annotation { "Feature Type Name" : "Feature", "Feature Type Description" : "" }
export const myFeature = defineFeature(function(context is Context, id is Id, definition is map)
    precondition{}
    {
        {
            var Q0;
            Q0=qCreatedBy(makeId("Front.planeOp"),FACE);
            var sketch = newSketch(context, id + "F0", { "sketchPlane" : qUnion([Q0])});
            skLineSegment(sketch, "E0.bottom", {"start": v(50.8, -15.87) * mm, "end": v(-50.8, -15.88) * mm});
            skLineSegment(sketch, "E0.top", {"start": v(50.8, 15.88) * mm, "end": v(-50.8, 15.87) * mm});
            skLineSegment(sketch, "E0.left", {"start": v(50.8, -15.87) * mm, "end": v(50.8, 15.88) * mm});
            skLineSegment(sketch, "E0.right", {"start": v(-50.8, -15.88) * mm, "end": v(-50.8, 15.87) * mm});
            skPoint(sketch, "E0.middle", {"position": v(0, 0) * mm});
            skSolve(sketch);
        }
        {
            var Q0;
            Q0 = qSketchRegion(id + "F0", true);
            var Q1;
            Q1=makeQuery(id+"F0.imprint","IMPRINT",FACE,{"disambiguationData":[TD([[makeQuery(id+"F0.imprint","IMPRINT",EDGE,{"derivedFrom":sQuery(id+"F0.wireOp",EDGE,"E0.bottom")}),-1.0]])]});
            extrude(context, id + "F1", {"entities" : qUnion([Q0, Q1]), "depth" : 152.4 * mm, "offsetDistance" : 25.4 * mm});
        }
        {
            var Q0;
            Q0=makeQuery(id+"F1.opExtrude","CAP_FACE",FACE,{"disambiguationData":[OSD([sQuery(id+"F0.wireOp",EDGE,"E0.bottom"),sQuery(id+"F0.wireOp",EDGE,"E0.top"),sQuery(id+"F0.wireOp",EDGE,"E0.left"),sQuery(id+"F0.wireOp",EDGE,"E0.right")])],"isStart":false});
            var sketch = newSketch(context, id + "F2", { "sketchPlane" : qUnion([Q0])});
            skLineSegment(sketch, "E1", {"start": v(-50.8, 15.87) * mm, "end": v(-50.8, -9.53) * mm});
            skLineSegment(sketch, "E2", {"start": v(50.8, 15.88) * mm, "end": v(50.8, -9.52) * mm});
            skLineSegment(sketch, "E3", {"start": v(44.42, -9.52) * mm, "end": v(10.93, -9.52) * mm});
            skLineSegment(sketch, "E4", {"start": v(-50.8, -9.53) * mm, "end": v(-43.03, -9.53) * mm});
            skLineSegment(sketch, "E5", {"start": v(-43.03, -9.52) * mm, "end": v(-6.12, -9.52) * mm});
            skPoint(sketch, "E6", {"position": v(-43.03, -9.52) * mm});
            skPoint(sketch, "E7", {"position": v(-6.12, -9.52) * mm});
            skPoint(sketch, "E8", {"position": v(10.93, -9.52) * mm});
            skLineSegment(sketch, "E9", {"start": v(-50.8, -9.53) * mm, "end": v(44.42, -9.52) * mm});
            skPoint(sketch, "E10", {"position": v(44.42, -9.52) * mm});
            skLineSegment(sketch, "E11", {"start": v(-43.03, -9.52) * mm, "end": v(-36.68, -15.88) * mm});
            skLineSegment(sketch, "E12", {"start": v(-6.12, -9.52) * mm, "end": v(-12.47, -15.88) * mm});
            skLineSegment(sketch, "E13", {"start": v(10.93, -9.52) * mm, "end": v(17.28, -15.87) * mm});
            skLineSegment(sketch, "E14", {"start": v(44.42, -9.52) * mm, "end": v(38.07, -15.87) * mm});
            skSolve(sketch);
        }
        {
            var Q0;
            {var subQ2=sQuery(id+"F2.wireOp",EDGE,"E13");Q0=makeQuery(id+"F2.imprint","IMPRINT",FACE,{"disambiguationData":[TD([[makeQuery(id+"F2.imprint","IMPRINT",EDGE,{"derivedFrom":subQ2}),1.0]])]});}
            var Q1;
            {var subQ0=sQuery(id+"F2.wireOp",EDGE,"E11");Q1=makeQuery(id+"F2.imprint","IMPRINT",FACE,{"disambiguationData":[TD([[makeQuery(id+"F2.imprint","IMPRINT",EDGE,{"derivedFrom":subQ0}),1.0]])]});}
            extrude(context, id + "F3", {"entities" : qUnion([Q0, Q1]), "operationType" : NewBodyOperationType.REMOVE, "oppositeDirection" : true, "depth" : 19.05 * mm, "offsetDistance" : 25.4 * mm});
        }
        {
            var Q0;
            Q0=makeQuery(id+"F1.opExtrude","CAP_FACE",FACE,{"disambiguationData":[OSD([sQuery(id+"F0.wireOp",EDGE,"E0.bottom"),sQuery(id+"F0.wireOp",EDGE,"E0.top"),sQuery(id+"F0.wireOp",EDGE,"E0.left"),sQuery(id+"F0.wireOp",EDGE,"E0.right")])],"isStart":true});
            var sketch = newSketch(context, id + "F4", { "sketchPlane" : qUnion([Q0])});
            skLineSegment(sketch, "E15", {"start": v(-50.8, 15.88) * mm, "end": v(-50.8, -9.52) * mm});
            skLineSegment(sketch, "E16", {"start": v(-50.8, -9.52) * mm, "end": v(50.8, -9.52) * mm});
            skLineSegment(sketch, "E17", {"start": v(-50.8, -9.52) * mm, "end": v(-45.92, -9.52) * mm});
            skLineSegment(sketch, "E18", {"start": v(-45.92, -9.52) * mm, "end": v(-39.57, -15.87) * mm});
            skLineSegment(sketch, "E19", {"start": v(-50.8, -9.52) * mm, "end": v(-4.88, -9.52) * mm});
            skLineSegment(sketch, "E20", {"start": v(-4.88, -9.52) * mm, "end": v(-11.23, -15.87) * mm});
            skLineSegment(sketch, "E21", {"start": v(-50.8, -9.52) * mm, "end": v(4.88, -9.52) * mm});
            skLineSegment(sketch, "E22", {"start": v(4.88, -9.52) * mm, "end": v(11.23, -15.88) * mm});
            skLineSegment(sketch, "E23", {"start": v(-50.8, -9.52) * mm, "end": v(45.92, -9.52) * mm});
            skLineSegment(sketch, "E24", {"start": v(45.92, -9.52) * mm, "end": v(39.57, -15.88) * mm});
            skSolve(sketch);
        }
        {
            var Q0;
            {var subQ0=sQuery(id+"F4.wireOp",EDGE,"E18");Q0=makeQuery(id+"F4.imprint","IMPRINT",FACE,{"disambiguationData":[TD([[makeQuery(id+"F4.imprint","IMPRINT",EDGE,{"derivedFrom":subQ0}),1.0]])]});}
            var Q1;
            {var subQ0=sQuery(id+"F4.wireOp",EDGE,"E22");Q1=makeQuery(id+"F4.imprint","IMPRINT",FACE,{"disambiguationData":[TD([[makeQuery(id+"F4.imprint","IMPRINT",EDGE,{"derivedFrom":subQ0}),1.0]])]});}
            extrude(context, id + "F5", {"entities" : qUnion([Q0, Q1]), "operationType" : NewBodyOperationType.REMOVE, "oppositeDirection" : true, "depth" : 38.1 * mm, "offsetDistance" : 25.4 * mm});
        }
        {
            var Q0;
            Q0=makeQuery(id+"F1.opExtrude","CAP_FACE",FACE,{"disambiguationData":[OSD([sQuery(id+"F0.wireOp",EDGE,"E0.bottom"),sQuery(id+"F0.wireOp",EDGE,"E0.top"),sQuery(id+"F0.wireOp",EDGE,"E0.left"),sQuery(id+"F0.wireOp",EDGE,"E0.right")])],"isStart":false});
            var sketch = newSketch(context, id + "F6", { "sketchPlane" : qUnion([Q0])});
            skLineSegment(sketch, "E25", {"start": v(-50.8, 15.87) * mm, "end": v(-50.8, 6.88) * mm});
            skLineSegment(sketch, "E26", {"start": v(-50.8, 6.88) * mm, "end": v(50.8, 6.88) * mm});
            skLineSegment(sketch, "E27", {"start": v(-50.8, 6.88) * mm, "end": v(-40.74, 6.88) * mm});
            skLineSegment(sketch, "E28", {"start": v(-40.74, 6.88) * mm, "end": v(-31.75, 15.88) * mm});
            skLineSegment(sketch, "E29", {"start": v(-50.8, 6.88) * mm, "end": v(-50.8, -15.88) * mm});
            skLineSegment(sketch, "E30", {"start": v(50.8, 6.88) * mm, "end": v(50.8, -15.87) * mm});
            skLineSegment(sketch, "E31", {"start": v(50.8, -15.87) * mm, "end": v(50.8, 15.88) * mm});
            skLineSegment(sketch, "E32", {"start": v(-50.8, 6.88) * mm, "end": v(-10.06, 6.88) * mm});
            skLineSegment(sketch, "E33", {"start": v(-10.06, 6.88) * mm, "end": v(-19.05, 15.88) * mm});
            skLineSegment(sketch, "E34", {"start": v(-50.8, 6.88) * mm, "end": v(10.06, 6.88) * mm});
            skLineSegment(sketch, "E35", {"start": v(10.06, 6.88) * mm, "end": v(19.05, 15.88) * mm});
            skLineSegment(sketch, "E36", {"start": v(-50.8, 6.88) * mm, "end": v(40.74, 6.88) * mm});
            skLineSegment(sketch, "E37", {"start": v(40.74, 6.88) * mm, "end": v(31.75, 15.88) * mm});
            skSolve(sketch);
        }
        {
            var Q0;
            {var subQ0=sQuery(id+"F6.wireOp",EDGE,"E28");Q0=makeQuery(id+"F6.imprint","IMPRINT",FACE,{"disambiguationData":[TD([[makeQuery(id+"F6.imprint","IMPRINT",EDGE,{"derivedFrom":subQ0}),-1.0]])]});}
            var Q1;
            {var subQ0=sQuery(id+"F6.wireOp",EDGE,"E35");Q1=makeQuery(id+"F6.imprint","IMPRINT",FACE,{"disambiguationData":[TD([[makeQuery(id+"F6.imprint","IMPRINT",EDGE,{"derivedFrom":subQ0}),-1.0]])]});}
            extrude(context, id + "F7", {"entities" : qUnion([Q0, Q1]), "operationType" : NewBodyOperationType.REMOVE, "endBound" : BoundingType.THROUGH_ALL, "oppositeDirection" : true, "depth" : 25.4 * mm, "offsetDistance" : 25.4 * mm});
        }
        {
            var Q0;
            Q0=makeQuery(id+"F1.opExtrude","SWEPT_EDGE",EDGE,{"disambiguationData":[OSD([sQuery(id+"F0.wireOp",EDGE,"E0.top"),sQuery(id+"F0.wireOp",EDGE,"E0.right")])]});
            var Q1;
            Q1=makeQuery(id+"F1.opExtrude","SWEPT_EDGE",EDGE,{"disambiguationData":[OSD([sQuery(id+"F0.wireOp",EDGE,"E0.top"),sQuery(id+"F0.wireOp",EDGE,"E0.left")])]});
            var Q2;
            Q2=makeQuery(id+"F1.opExtrude","SWEPT_EDGE",EDGE,{"disambiguationData":[OSD([sQuery(id+"F0.wireOp",EDGE,"E0.bottom"),sQuery(id+"F0.wireOp",EDGE,"E0.right")])]});
            var Q3;
            Q3=makeQuery(id+"F1.opExtrude","SWEPT_EDGE",EDGE,{"disambiguationData":[OSD([sQuery(id+"F0.wireOp",EDGE,"E0.bottom"),sQuery(id+"F0.wireOp",EDGE,"E0.left")])]});
            chamfer(context, id + "F8", {"entities" : qUnion([Q0, Q1, Q2, Q3]), "width" : 6.35 * mm, "tangentPropagation" : true});
        }
        {
            var Q0;
            {var subQ2=sQuery(id+"F0.wireOp",EDGE,"E0.top");Q0=makeQuery(id+"F7.boolean.opBoolean","SPLIT",FACE,{"disambiguationData":[TD([makeQuery(id+"F7.opExtrude","SWEPT_FACE",FACE,{"disambiguationData":[OSD([sQuery(id+"F6.wireOp",EDGE,"E33")])]})])],"derivedFrom":makeQuery(id+"F1.opExtrude","SWEPT_FACE",FACE,{"disambiguationData":[OSD([subQ2])]})});}
            var sketch = newSketch(context, id + "F9", { "sketchPlane" : qUnion([Q0])});
            skPoint(sketch, "E38", {"position": v(-8.25, -12.67) * mm});
            skPoint(sketch, "E39", {"position": v(-8.25, -55.02) * mm});
            skPoint(sketch, "E40", {"position": v(-8.25, -97.36) * mm});
            skPoint(sketch, "E41", {"position": v(-8.25, -139.7) * mm});
            skCircle(sketch, "E42", {"center": v(-8.25, -12.67) * mm, "radius": 1.9 * mm});
            skCircle(sketch, "E43", {"center": v(-8.25, -12.67) * mm, "radius": 4.56 * mm});
            skCircle(sketch, "E44", {"center": v(-8.25, -55.02) * mm, "radius": 1.9 * mm});
            skCircle(sketch, "E45", {"center": v(-8.25, -55.02) * mm, "radius": 4.56 * mm});
            skCircle(sketch, "E46", {"center": v(-8.25, -97.36) * mm, "radius": 1.9 * mm});
            skCircle(sketch, "E47", {"center": v(-8.25, -97.36) * mm, "radius": 4.56 * mm});
            skCircle(sketch, "E48", {"center": v(-8.25, -139.7) * mm, "radius": 1.9 * mm});
            skCircle(sketch, "E49", {"center": v(-8.25, -139.7) * mm, "radius": 4.56 * mm});
            skLineSegment(sketch, "E50", {"start": v(0, 0) * mm, "end": v(0, -152.4) * mm});
            skPoint(sketch, "E51.MirrorP", {"position": v(8.25, -12.67) * mm});
            skCircle(sketch, "E52.MirrorC", {"center": v(8.25, -12.67) * mm, "radius": 1.9 * mm});
            skCircle(sketch, "E53.MirrorC", {"center": v(8.25, -12.67) * mm, "radius": 4.56 * mm});
            skPoint(sketch, "E54.MirrorP", {"position": v(8.25, -55.02) * mm});
            skCircle(sketch, "E55.MirrorC", {"center": v(8.25, -55.02) * mm, "radius": 1.9 * mm});
            skCircle(sketch, "E56.MirrorC", {"center": v(8.25, -97.36) * mm, "radius": 1.9 * mm});
            skCircle(sketch, "E57.MirrorC", {"center": v(8.25, -139.7) * mm, "radius": 1.9 * mm});
            skCircle(sketch, "E58.MirrorC", {"center": v(8.25, -139.7) * mm, "radius": 4.56 * mm});
            skCircle(sketch, "E59.MirrorC", {"center": v(8.25, -97.36) * mm, "radius": 4.56 * mm});
            skCircle(sketch, "E60.MirrorC", {"center": v(8.25, -55.02) * mm, "radius": 4.56 * mm});
            skSolve(sketch);
        }
        {
            var Q0;
            Q0=sQuery(id+"F9.wireOp",VERTEX,"E38");
            var Q1;
            Q1=sQuery(id+"F9.wireOp",VERTEX,"E39");
            var Q2;
            Q2=sQuery(id+"F9.wireOp",VERTEX,"E40");
            var Q3;
            Q3=sQuery(id+"F9.wireOp",VERTEX,"E41");
            var Q4;
            Q4=sQuery(id+"F9.wireOp",VERTEX,"E57.MirrorC.center");
            var Q5;
            Q5=sQuery(id+"F9.wireOp",VERTEX,"E56.MirrorC.center");
            var Q6;
            Q6=sQuery(id+"F9.wireOp",VERTEX,"E54.MirrorP");
            var Q7;
            Q7=sQuery(id+"F9.wireOp",VERTEX,"E51.MirrorP");
            var Q8;
            Q8=makeQuery(id+"F1.opExtrude","SWEPT_BODY",BODY,{"disambiguationData":[OSD([sQuery(id+"F0.wireOp",EDGE,"E0.bottom"),sQuery(id+"F0.wireOp",EDGE,"E0.top"),sQuery(id+"F0.wireOp",EDGE,"E0.left"),sQuery(id+"F0.wireOp",EDGE,"E0.right")])]});
            hole(context, id + "F10", {"style" : HoleStyle.C_SINK, "endStyle" : HoleEndStyle.BLIND, "holeDiameter" : 3.8 * mm, "cSinkDiameter" : 9.12 * mm, "cSinkAngle" : 82 * degree, "majorDiameter" : 6.35 * mm, "holeDepth" : 9.52 * mm, "isTappedThrough" : true, "tappedDepth" : 12.7 * mm, "tapClearance" : 3, "locations" : qUnion([Q0, Q1, Q2, Q3, Q4, Q5, Q6, Q7]), "scope" : qUnion([Q8])});
        }
        {
            var Q0;
            Q0=makeQuery(id+"F1.opExtrude","SWEPT_FACE",FACE,{"disambiguationData":[OSD([sQuery(id+"F0.wireOp",EDGE,"E0.right")])]});
            var sketch = newSketch(context, id + "F11", { "sketchPlane" : qUnion([Q0])});
            skLineSegment(sketch, "E61", {"start": v(0, 0) * mm, "end": v(19.05, 0) * mm});
            skLineSegment(sketch, "E62", {"start": v(0, 0) * mm, "end": v(133.35, 0) * mm});
            skSolve(sketch);
        }
        {
            var Q0;
            Q0=sQuery(id+"F11.wireOp",VERTEX,"E61.end");
            var Q1;
            Q1=sQuery(id+"F11.wireOp",VERTEX,"E62.end");
            var Q2;
            Q2=makeQuery(id+"F1.opExtrude","SWEPT_BODY",BODY,{"disambiguationData":[OSD([sQuery(id+"F0.wireOp",EDGE,"E0.bottom"),sQuery(id+"F0.wireOp",EDGE,"E0.top"),sQuery(id+"F0.wireOp",EDGE,"E0.left"),sQuery(id+"F0.wireOp",EDGE,"E0.right")])]});
            hole(context, id + "F12", {"style" : HoleStyle.C_BORE, "endStyle" : HoleEndStyle.BLIND, "holeDiameter" : 6.35 * mm, "cBoreDiameter" : 9.52 * mm, "cBoreDepth" : 6.35 * mm, "majorDiameter" : 6.35 * mm, "holeDepth" : 25.4 * mm, "isTappedThrough" : true, "tappedDepth" : 12.7 * mm, "tapClearance" : 3, "locations" : qUnion([Q0, Q1]), "scope" : qUnion([Q2])});
        }
        {
            var Q0;
            Q0=makeQuery(id+"F1.opExtrude","SWEPT_FACE",FACE,{"disambiguationData":[OSD([sQuery(id+"F0.wireOp",EDGE,"E0.left")])]});
            var sketch = newSketch(context, id + "F13", { "sketchPlane" : qUnion([Q0])});
            skLineSegment(sketch, "E63", {"start": v(0, 0) * mm, "end": v(-19.05, 0) * mm});
            skLineSegment(sketch, "E64", {"start": v(0, 0) * mm, "end": v(-133.35, 0) * mm});
            skPoint(sketch, "E65", {"position": v(-133.35, 0) * mm});
            skPoint(sketch, "E66", {"position": v(-19.05, 0) * mm});
            skSolve(sketch);
        }
        {
            var Q0;
            Q0=sQuery(id+"F13.wireOp",VERTEX,"E65");
            var Q1;
            Q1=sQuery(id+"F13.wireOp",VERTEX,"E66");
            var Q2;
            Q2=makeQuery(id+"F1.opExtrude","SWEPT_BODY",BODY,{"disambiguationData":[OSD([sQuery(id+"F0.wireOp",EDGE,"E0.bottom"),sQuery(id+"F0.wireOp",EDGE,"E0.top"),sQuery(id+"F0.wireOp",EDGE,"E0.left"),sQuery(id+"F0.wireOp",EDGE,"E0.right")])]});
            hole(context, id + "F14", {"style" : HoleStyle.C_BORE, "endStyle" : HoleEndStyle.BLIND, "holeDiameter" : 6.35 * mm, "cBoreDiameter" : 9.52 * mm, "cBoreDepth" : 6.35 * mm, "majorDiameter" : 6.35 * mm, "holeDepth" : 25.4 * mm, "isTappedThrough" : true, "tappedDepth" : 12.7 * mm, "tapClearance" : 3, "locations" : qUnion([Q0, Q1]), "scope" : qUnion([Q2])});
        }
        {
            var Q0;
            Q0=makeQuery(id+"F1.opExtrude","SWEPT_FACE",FACE,{"disambiguationData":[OSD([sQuery(id+"F0.wireOp",EDGE,"E0.bottom")])]});
            var sketch = newSketch(context, id + "F15", { "sketchPlane" : qUnion([Q0])});
            skText(sketch, "E67", { "text": "Parker Magahey\nCTAE Room 711\nGTID: 5590040108", "fontName": "OpenSans-Regular.ttf"});
            const initialGuessF15  = {"E67": [-0.04015, 0.12282, 1, 0, 0.00629]};
            skSetInitialGuess(sketch, initialGuessF15);
            skSolve(sketch);
        }
        {
            var Q0;
            Q0 = qSketchRegion(id + "F15", true);
            extrude(context, id + "F16", {"entities" : qUnion([Q0]), "operationType" : NewBodyOperationType.REMOVE, "oppositeDirection" : true, "depth" : 3.8 * mm, "offsetDistance" : 25.4 * mm});
        }
    });